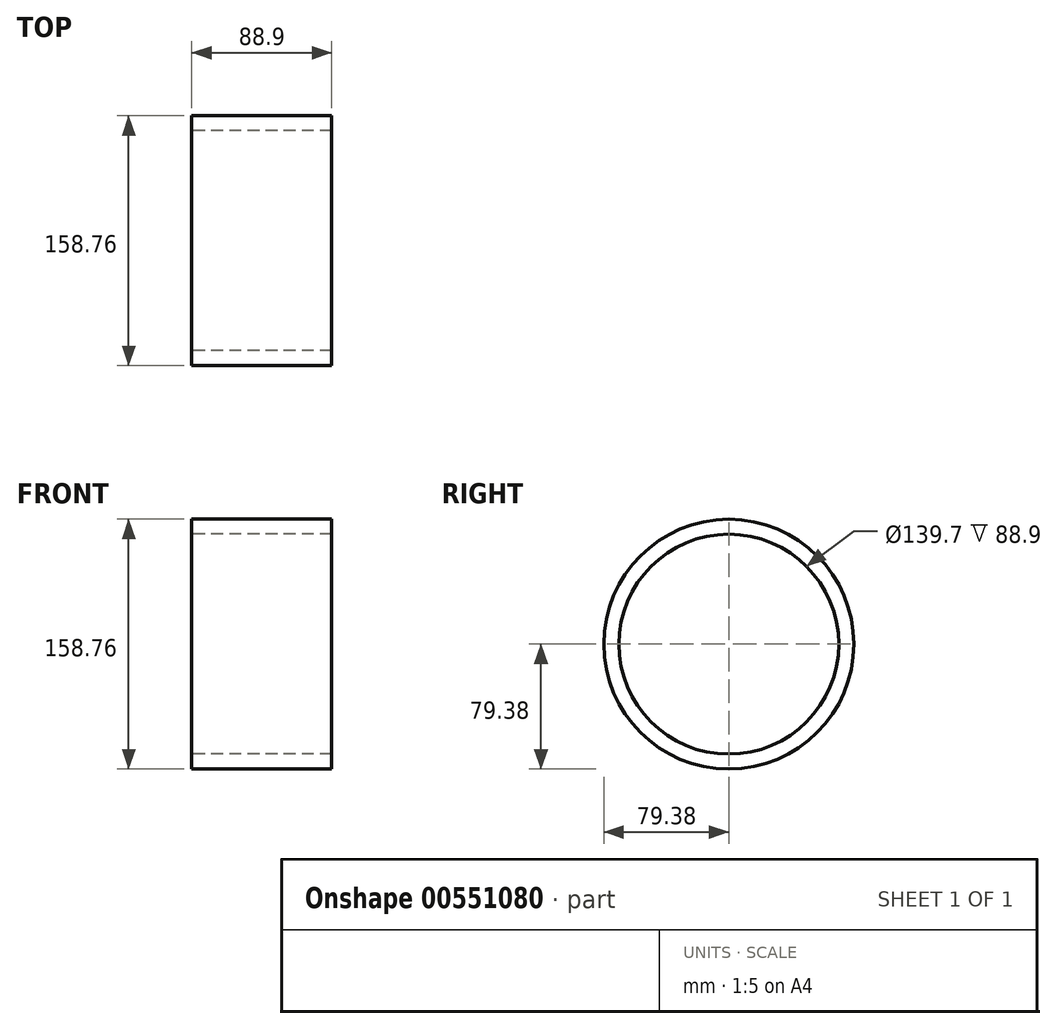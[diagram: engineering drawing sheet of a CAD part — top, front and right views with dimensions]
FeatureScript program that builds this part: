
annotation { "Feature Type Name" : "Feature", "Feature Type Description" : "" }
export const myFeature = defineFeature(function(context is Context, id is Id, definition is map)
    precondition{}
    {
        {
            var Q0;
            Q0=qCreatedBy(makeId("Right.planeOp"),FACE);
            var sketch = newSketch(context, id + "F0", { "sketchPlane" : qUnion([Q0])});
            skCircle(sketch, "E0", {"center": v(0, 0) * mm, "radius": 69.85 * mm});
            skCircle(sketch, "E1", {"center": v(0, 0) * mm, "radius": 79.38 * mm});
            skSolve(sketch);
        }
        {
            var Q0;
            Q0=qSketchRegion(id+"F0",true);
            extrude(context, id + "F1", {"entities" : qUnion([Q0]), "endBound" : BoundingType.SYMMETRIC, "depth" : 88.9 * mm});
        }
    });
